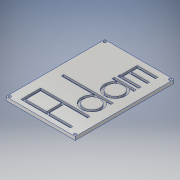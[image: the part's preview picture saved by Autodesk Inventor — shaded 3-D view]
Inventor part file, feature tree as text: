
AUTODESK INVENTOR PART (.ipt)
format: ipt  version: 2016 (Build 200138000, 138)  size: 274,944 bytes
history: native  units: in
note: dims shown in document units (in); Inventor stores cm internally (conversion verified against a paired STEP export)
features: sketch x16, extrude x8
ambient origin geometry x8: Origin, YZ Plane, XZ Plane, XY Plane, X Axis, Y Axis, Z Axis, Center Point
bodies: Solid1 (feature_tree)
feature tree (24):
  sketch  "Sketch1"  dims[d0=10.0in d1=7.0in]
  sketch  "Sketch2"  dims[d2=0.35in d3=0.0in d4=0.25in]
  extrude  "Extrusion1"  Depth=7.0in
  sketch  "Sketch3"  dims[d5=0.5in d6=1.0in]
  sketch  "Sketch4"  dims[d7=1.0in d8=0.25in]
  extrude  "Extrusion2"  Depth=0.25in
  sketch  "Sketch5"  dims[d10=5.0in d11=0.25in]
  sketch  "Sketch6"  dims[d12=2.0in d13=0.25in]
  extrude  "Extrusion3"  Depth=1.0in
  sketch  "Sketch7"  dims[d14=2.375in d15=2.375in]
  sketch  "Sketch9"  dims[d16=0.2in d17=0.0in d18=2.1in]
  extrude  "Extrusion4"  Depth=0.25in
  sketch  "Sketch12"  dims[d19=0.25in]
  extrude  "Extrusion5"  Depth=0.25in
  sketch  "Sketch15"  dims[d22=0.25in]
  sketch  "Sketch16"  dims[d23=0.85in]
  sketch  "Sketch14"  dims[d21=1.0in]
  extrude  "Extrusion6"  Depth=0.25in
  sketch  "Sketch19"  dims[d24=3.946in]
  sketch  "Sketch21"  dims[d25=2.054in]
  extrude  "Extrusion7"  Depth=2.375in
  extrude  "Extrusion8"  Depth=2.1in
  sketch  "Sketch13"  dims[d20=5.0in]
  sketch  "Sketch22"  dims[d26=0.2in d27=0.0in d31=1.0in d35=1.25in d37=1.1in d39=1.1in d40=2.5in d42=1.0in d43=1.054in d44=1.054in d45=1.25in d46=0.25in d48=0.2in d49=0.0in d53=0.25in d54=1.0in d55=2.2in d56=2.07in d57=0.2in d58=0.0in d59=0.25in d60=0.25in d61=0.25in d62=0.6in d63=0.25in d64=0.6in d65=0.25in d66=0.25in d67=0.2in d68=0.0in d69=0.25in d70=0.2in d71=0.2in d72=0.25in d73=0.2in d74=0.2in d75=0.25in d76=0.2in d77=0.2in d78=0.25in d79=0.2in d80=0.2in d81=1.0in d82=0.0in d83=1.0in d84=0.0in]
